# Revit family: duo-mini-1
name_source: partatom
category: Lighting Fixtures
units: mm (PartAtom-declared; Revit-internal decimal feet)

## family parameters
Always vertical = Yes
Cut with Voids When Loaded = No
Host = Ceiling
Light Source = Yes
OmniClass Number = 23.80.70.11
OmniClass Title = Luminaries for Internal Lighting
Part Type = Normal
Room Calculation Point = No
Round Connector Dimension = Use Diameter
Shared = No

## types (6) — shared parameters
Apparent Load = 0 VA
Color Filter = 16777215
Default Elevation = 0.00"
Description = Downlight
Dimming Lamp Color Temperature Shift = <None>
Emit Shape Visible in Rendering = No
Glass = Light Panel
Load Classification = Other
Manufacturer = ARON
Poles = 1
Product Documentation Link = https://www.aronlighting.com
Specification = https://www.aronlighting.com
Tilt Angle = 60.00°
Voltage = 120 V
Width = 6.75"

## per-type parameters (varying)
| type | Case | Dimensions (W x L) | Emit from Rectangle Length | Emit from Rectangle Width | Length | Model | Photometric Web File | URL |
| DM12 W | White | 6.75" x 11.75" | 6.70" | 11.75" | 11.75" | DM12 W | DuoT1-12IN-2000-B2-3000K-80-UNV-DM.ies | http://www.aronlighting.com |
| DM12 BLK | Black | 6.75" x 11.75" | 6.70" | 11.75" | 11.75" | DM12 BLK | DuoT1-12IN-2000-B2-3000K-80-UNV-DM.ies | http://www.aronlighting.com |
| DM6 BLK | Black | 6.75" x 6.75" | 6.75" | 6.75" | 6.75" | DM7 BLK | DuoT1-6IN-2000-B2-3000K-80-UNV-DM.ies | https://www.aronlighting.com |
| DM6 W | White | 6.75" x 6.75" | 6.75" | 6.75" | 6.75" | DM7 W | DuoT1-6IN-2000-B2-3000K-80-UNV-DM.ies | https://www.aronlighting.com |
| DM9 W | White | 6.75" x 9.75" | 6.75" | 9.75" | 9.75" | DM10 W | DuoT1-9IN-2000-B2-3000K-80-UNV-DM.ies | http://www.aronlighting.com |
| DM9 BLK | Black | 6.75" x 9.75" | 6.75" | 9.75" | 9.75" | DM10 BLK | DuoT1-9IN-2000-B2-3000K-80-UNV-DM.ies | http://www.aronlighting.com |

## geometry (parser evidence)
native form markers: Sweep x2
no freeform markers — native parametric forms only
